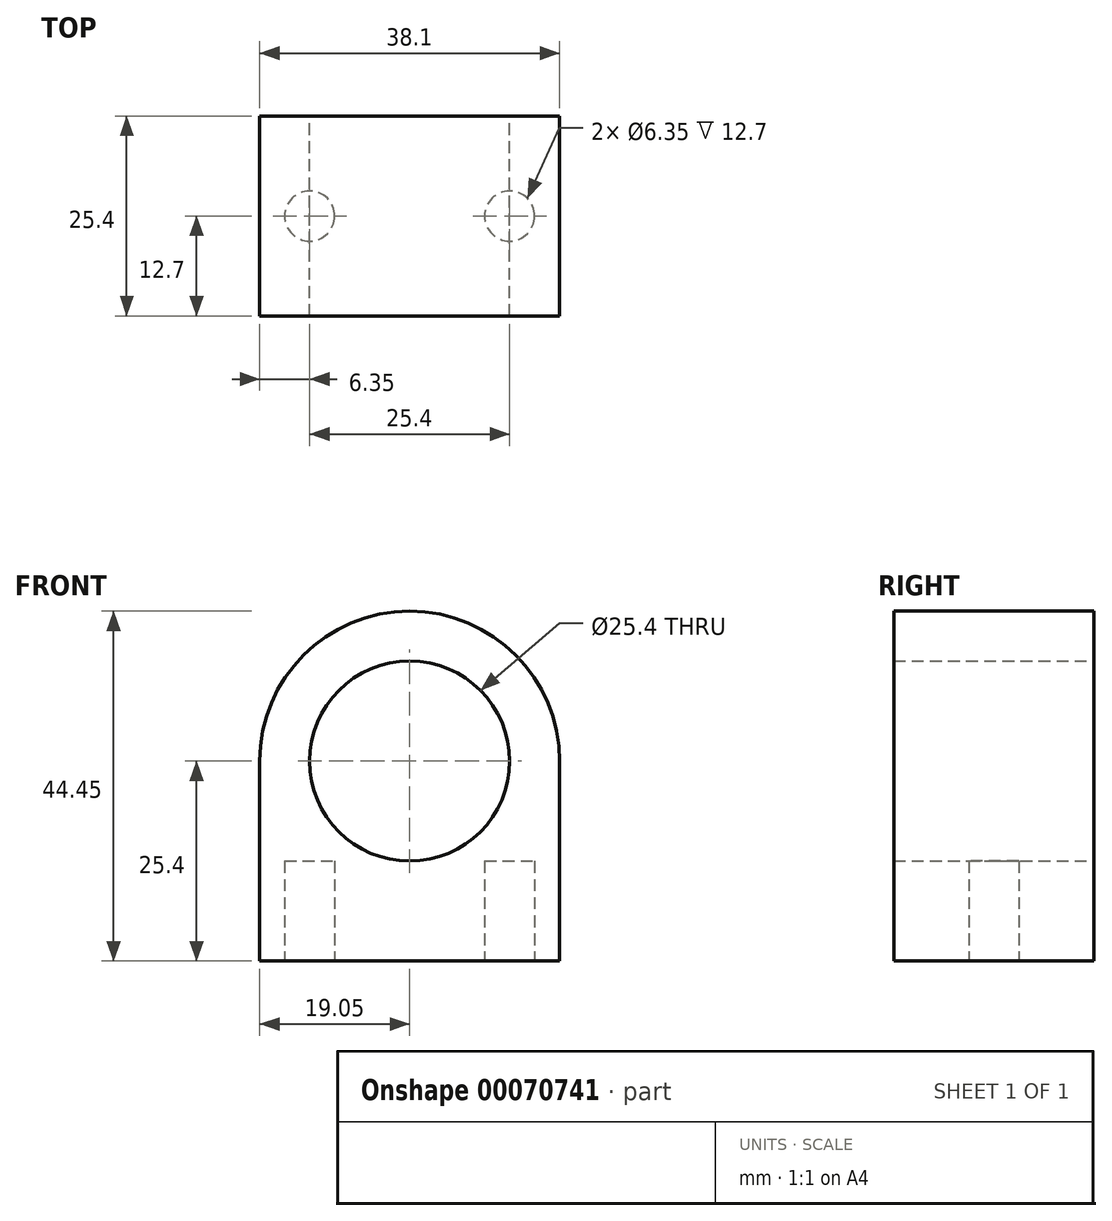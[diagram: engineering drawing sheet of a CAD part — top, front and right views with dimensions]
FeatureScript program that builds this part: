
annotation { "Feature Type Name" : "Feature", "Feature Type Description" : "" }
export const myFeature = defineFeature(function(context is Context, id is Id, definition is map)
    precondition{}
    {
        {
            var Q0;
            Q0=qCreatedBy(makeId("Front.planeOp"),FACE);
            var sketch = newSketch(context, id + "F0", { "sketchPlane" : qUnion([Q0])});
            skLineSegment(sketch, "E0.bottom", {"start": v(0, 0) * mm, "end": v(38.1, 0) * mm});
            skLineSegment(sketch, "E0.top", {"start": v(0, 25.4) * mm, "end": v(38.1, 25.4) * mm});
            skLineSegment(sketch, "E0.left", {"start": v(0, 0) * mm, "end": v(0, 25.4) * mm});
            skLineSegment(sketch, "E0.right", {"start": v(38.1, 0) * mm, "end": v(38.1, 25.4) * mm});
            skArc(sketch, "E1", {"start": v(38.1, 25.4) * mm, "mid": v(19.05, 44.45) * mm, "end": v(0, 25.4) * mm});
            skCircle(sketch, "E2", {"center": v(19.05, 25.4) * mm, "radius": 12.7 * mm});
            skSolve(sketch);
        }
        {
            var Q0;
            Q0=makeQuery(id+"F0.imprint","IMPRINT",FACE,{"disambiguationData":[TD([[makeQuery(id+"F0.imprint","IMPRINT",EDGE,{"derivedFrom":sQuery(id+"F0.wireOp",EDGE,"E0.bottom")}),1.0]])]});
            var Q1;
            {var subQ0=sQuery(id+"F0.wireOp",EDGE,"E1");Q1=makeQuery(id+"F0.imprint","IMPRINT",FACE,{"disambiguationData":[TD([[makeQuery(id+"F0.imprint","IMPRINT",EDGE,{"derivedFrom":subQ0}),1.0]])]});}
            extrude(context, id + "F1", {"entities" : qUnion([Q0, Q1]), "depth" : 25.4 * mm});
        }
        {
            var Q0;
            Q0=makeQuery(id+"F1.opExtrude","SWEPT_FACE",FACE,{"disambiguationData":[OSD([sQuery(id+"F0.wireOp",EDGE,"E0.bottom")])]});
            var sketch = newSketch(context, id + "F2", { "sketchPlane" : qUnion([Q0])});
            skCircle(sketch, "E3", {"center": v(6.35, 12.7) * mm, "radius": 3.18 * mm});
            skPoint(sketch, "E3.centerSnap0", {"position": v(0, 12.7) * mm});
            skCircle(sketch, "E4", {"center": v(31.75, 12.7) * mm, "radius": 3.18 * mm});
            skSolve(sketch);
        }
        {
            var Q0;
            Q0=makeQuery(id+"F2.imprint","IMPRINT",FACE,{"disambiguationData":[TD([[makeQuery(id+"F2.imprint","IMPRINT",EDGE,{"derivedFrom":sQuery(id+"F2.wireOp",EDGE,"E3")}),1.0]])]});
            var Q1;
            Q1=makeQuery(id+"F2.imprint","IMPRINT",FACE,{"disambiguationData":[TD([[makeQuery(id+"F2.imprint","IMPRINT",EDGE,{"derivedFrom":sQuery(id+"F2.wireOp",EDGE,"E4")}),1.0]])]});
            extrude(context, id + "F3", {"entities" : qUnion([Q0, Q1]), "operationType" : NewBodyOperationType.REMOVE, "oppositeDirection" : true, "depth" : 12.7 * mm});
        }
    });
